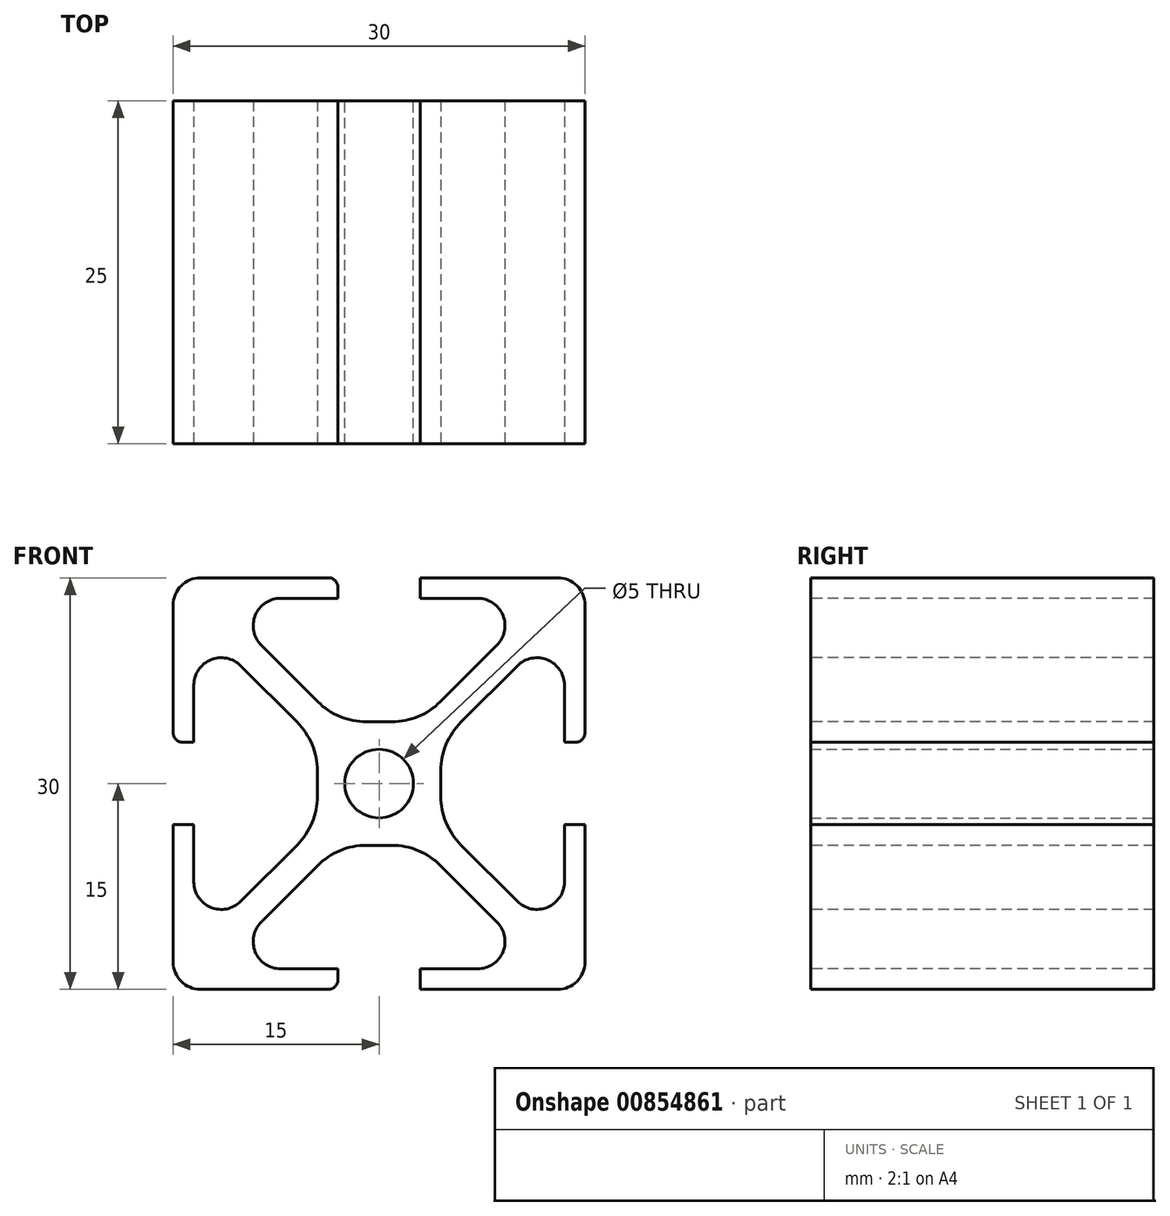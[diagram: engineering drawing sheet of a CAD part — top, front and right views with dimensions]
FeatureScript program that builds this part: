
annotation { "Feature Type Name" : "Feature", "Feature Type Description" : "" }
export const myFeature = defineFeature(function(context is Context, id is Id, definition is map)
    precondition{}
    {
        {
            var Q0;
            Q0=qCreatedBy(makeId("Front.planeOp"),FACE);
            var sketch = newSketch(context, id + "F0", { "sketchPlane" : qUnion([Q0])});
            skLineSegment(sketch, "E0.bottom", {"start": v(15, -15) * mm, "end": v(-15, -15) * mm});
            skLineSegment(sketch, "E0.top", {"start": v(15, 15) * mm, "end": v(-15, 15) * mm});
            skLineSegment(sketch, "E0.left", {"start": v(15, -15) * mm, "end": v(15, 15) * mm});
            skLineSegment(sketch, "E0.right", {"start": v(-15, -15) * mm, "end": v(-15, 15) * mm});
            skPoint(sketch, "E0.middle", {"position": v(0, 0) * mm});
            skCircle(sketch, "E1", {"center": v(0, 0) * mm, "radius": 2.5 * mm});
            skSolve(sketch);
        }
        {
            var Q0;
            Q0 = qSketchRegion(id + "F0", true);
            extrude(context, id + "F1", {"entities" : qUnion([Q0]), "endBound" : BoundingType.SYMMETRIC, "depth" : 25 * mm, "offsetDistance" : 25 * mm});
        }
        {
            var Q0;
            Q0=makeQuery(id+"F1.opExtrude","SWEPT_EDGE",EDGE,{"disambiguationData":[OSD([sQuery(id+"F0.wireOp",EDGE,"E0.top"),sQuery(id+"F0.wireOp",EDGE,"E0.left")])]});
            var Q1;
            Q1=makeQuery(id+"F1.opExtrude","SWEPT_EDGE",EDGE,{"disambiguationData":[OSD([sQuery(id+"F0.wireOp",EDGE,"E0.top"),sQuery(id+"F0.wireOp",EDGE,"E0.right")])]});
            var Q2;
            Q2=makeQuery(id+"F1.opExtrude","SWEPT_EDGE",EDGE,{"disambiguationData":[OSD([sQuery(id+"F0.wireOp",EDGE,"E0.bottom"),sQuery(id+"F0.wireOp",EDGE,"E0.right")])]});
            var Q3;
            Q3=makeQuery(id+"F1.opExtrude","SWEPT_EDGE",EDGE,{"disambiguationData":[OSD([sQuery(id+"F0.wireOp",EDGE,"E0.bottom"),sQuery(id+"F0.wireOp",EDGE,"E0.left")])]});
            fillet(context, id + "F2", {"entities" : qUnion([Q0, Q1, Q2, Q3]), "radius" : 2 * mm, "tangentPropagation" : true, "allowEdgeOverflow" : false});
        }
        {
            var Q0;
            Q0=makeQuery(id+"F1.opExtrude","CAP_FACE",FACE,{"disambiguationData":[OSD([sQuery(id+"F0.wireOp",EDGE,"E0.bottom"),sQuery(id+"F0.wireOp",EDGE,"E0.top"),sQuery(id+"F0.wireOp",EDGE,"E0.left"),sQuery(id+"F0.wireOp",EDGE,"E0.right"),sQuery(id+"F0.wireOp",EDGE,"E1")])],"isStart":false});
            var sketch = newSketch(context, id + "F3", { "sketchPlane" : qUnion([Q0])});
            skPoint(sketch, "E2.middle", {"position": v(0, 0) * mm});
            skLineSegment(sketch, "E3.left", {"start": v(4.5, 3) * mm, "end": v(4.5, -3) * mm});
            skLineSegment(sketch, "E4.bottom", {"start": v(-3, 4.5) * mm, "end": v(3, 4.5) * mm});
            skLineSegment(sketch, "E4.top", {"start": v(-3, 15) * mm, "end": v(3, 15) * mm});
            skLineSegment(sketch, "E4.left", {"start": v(-3, 4.5) * mm, "end": v(-3, 15) * mm});
            skLineSegment(sketch, "E4.right", {"start": v(3, 4.5) * mm, "end": v(3, 15) * mm});
            skLineSegment(sketch, "E5.bottom", {"start": v(4.5, 3) * mm, "end": v(15, 3) * mm});
            skLineSegment(sketch, "E5.top", {"start": v(4.5, -3) * mm, "end": v(15, -3) * mm});
            skLineSegment(sketch, "E5.right", {"start": v(15, 3) * mm, "end": v(15, -3) * mm});
            skLineSegment(sketch, "E6.bottom", {"start": v(3, -4.5) * mm, "end": v(-3, -4.5) * mm});
            skLineSegment(sketch, "E6.top", {"start": v(3, -15) * mm, "end": v(-3, -15) * mm});
            skLineSegment(sketch, "E6.left", {"start": v(3, -4.5) * mm, "end": v(3, -15) * mm});
            skLineSegment(sketch, "E6.right", {"start": v(-3, -4.5) * mm, "end": v(-3, -15) * mm});
            skLineSegment(sketch, "E7.bottom", {"start": v(-4.5, -3) * mm, "end": v(-15, -3) * mm});
            skLineSegment(sketch, "E7.top", {"start": v(-4.5, 3) * mm, "end": v(-15, 3) * mm});
            skLineSegment(sketch, "E7.left", {"start": v(-4.5, -3) * mm, "end": v(-4.5, 3) * mm});
            skLineSegment(sketch, "E7.right", {"start": v(-15, -3) * mm, "end": v(-15, 3) * mm});
            skSolve(sketch);
        }
        {
            var Q0;
            Q0 = qSketchRegion(id + "F3", true);
            extrude(context, id + "F4", {"entities" : qUnion([Q0]), "operationType" : NewBodyOperationType.REMOVE, "oppositeDirection" : true, "depth" : 25 * mm, "offsetDistance" : 25 * mm});
        }
        {
            var Q0;
            Q0 = qSketchRegion(id + "F3", true);
            extrude(context, id + "F5", {"entities" : qUnion([Q0]), "operationType" : NewBodyOperationType.REMOVE, "oppositeDirection" : true, "depth" : 25 * mm, "offsetDistance" : 25 * mm});
        }
        {
            var Q0;
            Q0=makeQuery(id+"F1.opExtrude","CAP_FACE",FACE,{"disambiguationData":[OSD([sQuery(id+"F0.wireOp",EDGE,"E0.bottom"),sQuery(id+"F0.wireOp",EDGE,"E0.top"),sQuery(id+"F0.wireOp",EDGE,"E0.left"),sQuery(id+"F0.wireOp",EDGE,"E0.right"),sQuery(id+"F0.wireOp",EDGE,"E1")])],"isStart":false});
            var sketch = newSketch(context, id + "F6", { "sketchPlane" : qUnion([Q0])});
            skPoint(sketch, "E8.middle", {"position": v(0, 0) * mm});
            skPoint(sketch, "E9.middle", {"position": v(9, 9) * mm});
            skLineSegment(sketch, "E10", {"start": v(3, 4.5) * mm, "end": v(12, 13.5) * mm});
            skLineSegment(sketch, "E11", {"start": v(4.5, 3) * mm, "end": v(13.5, 12) * mm});
            skLineSegment(sketch, "E12", {"start": v(13.5, 3) * mm, "end": v(13.5, 12) * mm});
            skLineSegment(sketch, "E13", {"start": v(3, 13.5) * mm, "end": v(12, 13.5) * mm});
            skLineSegment(sketch, "E14.MirrorCS", {"start": v(3, -13.5) * mm, "end": v(12, -13.5) * mm});
            skLineSegment(sketch, "E15.MirrorCS", {"start": v(3, -4.5) * mm, "end": v(12, -13.5) * mm});
            skLineSegment(sketch, "E16.MirrorCS", {"start": v(4.5, -3) * mm, "end": v(13.5, -12) * mm});
            skLineSegment(sketch, "E17.MirrorCS", {"start": v(13.5, -3) * mm, "end": v(13.5, -12) * mm});
            skLineSegment(sketch, "E18.MirrorCS", {"start": v(-3, 13.5) * mm, "end": v(-12, 13.5) * mm});
            skLineSegment(sketch, "E19.MirrorCS", {"start": v(-3, 4.5) * mm, "end": v(-12, 13.5) * mm});
            skLineSegment(sketch, "E20.MirrorCS", {"start": v(-4.5, 3) * mm, "end": v(-13.5, 12) * mm});
            skLineSegment(sketch, "E21.MirrorCS", {"start": v(-13.5, 3) * mm, "end": v(-13.5, 12) * mm});
            skLineSegment(sketch, "E22.MirrorCS", {"start": v(-4.5, -3) * mm, "end": v(-13.5, -12) * mm});
            skLineSegment(sketch, "E23.MirrorCS", {"start": v(-3, -4.5) * mm, "end": v(-12, -13.5) * mm});
            skLineSegment(sketch, "E24.MirrorCS", {"start": v(-3, -13.5) * mm, "end": v(-12, -13.5) * mm});
            skLineSegment(sketch, "E25.MirrorCS", {"start": v(-13.5, -3) * mm, "end": v(-13.5, -12) * mm});
            skLineSegment(sketch, "E26", {"start": v(-13.5, 3) * mm, "end": v(-4.5, 3) * mm});
            skLineSegment(sketch, "E27", {"start": v(-3, 4.5) * mm, "end": v(-3, 13.5) * mm});
            skLineSegment(sketch, "E28", {"start": v(3, 13.5) * mm, "end": v(3, 4.5) * mm});
            skLineSegment(sketch, "E29", {"start": v(4.5, 3) * mm, "end": v(13.5, 3) * mm});
            skLineSegment(sketch, "E30", {"start": v(13.5, -3) * mm, "end": v(4.5, -3) * mm});
            skLineSegment(sketch, "E31", {"start": v(3, -4.5) * mm, "end": v(3, -13.5) * mm});
            skLineSegment(sketch, "E32", {"start": v(-3, -13.5) * mm, "end": v(-3, -4.5) * mm});
            skLineSegment(sketch, "E33", {"start": v(-4.5, -3) * mm, "end": v(-13.5, -3) * mm});
            skSolve(sketch);
        }
        {
            var Q0;
            Q0 = qSketchRegion(id + "F6", true);
            extrude(context, id + "F7", {"entities" : qUnion([Q0]), "operationType" : NewBodyOperationType.REMOVE, "oppositeDirection" : true, "depth" : 25 * mm, "offsetDistance" : 25 * mm});
        }
        {
            var Q0;
            Q0=makeQuery(id+"F7.boolean.opBoolean","COPY",EDGE,{"derivedFrom":makeQuery(id+"F7.opExtrude","SWEPT_EDGE",EDGE,{"disambiguationData":[OSD([sQuery(id+"F6.wireOp",EDGE,"E23.MirrorCS"),sQuery(id+"F6.wireOp",EDGE,"E24.MirrorCS")])]})});
            var Q1;
            Q1=makeQuery(id+"F7.boolean.opBoolean","COPY",EDGE,{"derivedFrom":makeQuery(id+"F7.opExtrude","SWEPT_EDGE",EDGE,{"disambiguationData":[OSD([sQuery(id+"F6.wireOp",EDGE,"E14.MirrorCS"),sQuery(id+"F6.wireOp",EDGE,"E15.MirrorCS")])]})});
            var Q2;
            Q2=makeQuery(id+"F7.boolean.opBoolean","COPY",EDGE,{"derivedFrom":makeQuery(id+"F7.opExtrude","SWEPT_EDGE",EDGE,{"disambiguationData":[OSD([sQuery(id+"F6.wireOp",EDGE,"E16.MirrorCS"),sQuery(id+"F6.wireOp",EDGE,"E17.MirrorCS")])]})});
            var Q3;
            Q3=makeQuery(id+"F7.boolean.opBoolean","COPY",EDGE,{"derivedFrom":makeQuery(id+"F7.opExtrude","SWEPT_EDGE",EDGE,{"disambiguationData":[OSD([sQuery(id+"F6.wireOp",EDGE,"E22.MirrorCS"),sQuery(id+"F6.wireOp",EDGE,"E25.MirrorCS")])]})});
            var Q4;
            Q4=makeQuery(id+"F7.boolean.opBoolean","COPY",EDGE,{"derivedFrom":makeQuery(id+"F7.opExtrude","SWEPT_EDGE",EDGE,{"disambiguationData":[OSD([sQuery(id+"F6.wireOp",EDGE,"E11"),sQuery(id+"F6.wireOp",EDGE,"E12")])]})});
            var Q5;
            Q5=makeQuery(id+"F7.boolean.opBoolean","COPY",EDGE,{"derivedFrom":makeQuery(id+"F7.opExtrude","SWEPT_EDGE",EDGE,{"disambiguationData":[OSD([sQuery(id+"F6.wireOp",EDGE,"E10"),sQuery(id+"F6.wireOp",EDGE,"E13")])]})});
            var Q6;
            Q6=makeQuery(id+"F7.boolean.opBoolean","COPY",EDGE,{"derivedFrom":makeQuery(id+"F7.opExtrude","SWEPT_EDGE",EDGE,{"disambiguationData":[OSD([sQuery(id+"F6.wireOp",EDGE,"E20.MirrorCS"),sQuery(id+"F6.wireOp",EDGE,"E21.MirrorCS")])]})});
            var Q7;
            Q7=makeQuery(id+"F7.boolean.opBoolean","COPY",EDGE,{"derivedFrom":makeQuery(id+"F7.opExtrude","SWEPT_EDGE",EDGE,{"disambiguationData":[OSD([sQuery(id+"F6.wireOp",EDGE,"E18.MirrorCS"),sQuery(id+"F6.wireOp",EDGE,"E19.MirrorCS")])]})});
            fillet(context, id + "F8", {"entities" : qUnion([Q0, Q1, Q2, Q3, Q4, Q5, Q6, Q7]), "radius" : 2 * mm, "tangentPropagation" : true, "allowEdgeOverflow" : false});
        }
        {
            var Q0;
            Q0=makeQuery(id+"F7.boolean.opBoolean","COPY",EDGE,{"derivedFrom":makeQuery(id+"F7.opExtrude","SWEPT_EDGE",EDGE,{"disambiguationData":[OSD([sQuery(id+"F3.wireOp",EDGE,"E5.bottom"),sQuery(id+"F6.wireOp",EDGE,"E12"),sQuery(id+"F6.wireOp",EDGE,"E29")])]})});
            var Q1;
            Q1=makeQuery(id+"F4.boolean.opBoolean","COPY",EDGE,{"derivedFrom":makeQuery(id+"F4.opExtrude","SWEPT_EDGE",EDGE,{"disambiguationData":[OSD([sQuery(id+"F0.wireOp",EDGE,"E0.left"),sQuery(id+"F3.wireOp",EDGE,"E5.bottom"),sQuery(id+"F3.wireOp",EDGE,"E5.right")])]})});
            var Q2;
            Q2=makeQuery(id+"F4.boolean.opBoolean","COPY",EDGE,{"derivedFrom":makeQuery(id+"F4.opExtrude","SWEPT_EDGE",EDGE,{"disambiguationData":[OSD([sQuery(id+"F0.wireOp",EDGE,"E0.left"),sQuery(id+"F3.wireOp",EDGE,"E5.top"),sQuery(id+"F3.wireOp",EDGE,"E5.right")])]})});
            var Q3;
            Q3=makeQuery(id+"F7.boolean.opBoolean","COPY",EDGE,{"derivedFrom":makeQuery(id+"F7.opExtrude","SWEPT_EDGE",EDGE,{"disambiguationData":[OSD([sQuery(id+"F3.wireOp",EDGE,"E5.top"),sQuery(id+"F6.wireOp",EDGE,"E17.MirrorCS"),sQuery(id+"F6.wireOp",EDGE,"E30")])]})});
            var Q4;
            Q4=makeQuery(id+"F4.boolean.opBoolean","COPY",EDGE,{"derivedFrom":makeQuery(id+"F4.opExtrude","SWEPT_EDGE",EDGE,{"disambiguationData":[OSD([sQuery(id+"F0.wireOp",EDGE,"E0.bottom"),sQuery(id+"F3.wireOp",EDGE,"E6.top"),sQuery(id+"F3.wireOp",EDGE,"E6.left")])]})});
            var Q5;
            Q5=makeQuery(id+"F4.boolean.opBoolean","COPY",EDGE,{"derivedFrom":makeQuery(id+"F4.opExtrude","SWEPT_EDGE",EDGE,{"disambiguationData":[OSD([sQuery(id+"F0.wireOp",EDGE,"E0.bottom"),sQuery(id+"F3.wireOp",EDGE,"E6.top"),sQuery(id+"F3.wireOp",EDGE,"E6.right")])]})});
            var Q6;
            Q6=makeQuery(id+"F7.boolean.opBoolean","COPY",EDGE,{"derivedFrom":makeQuery(id+"F7.opExtrude","SWEPT_EDGE",EDGE,{"disambiguationData":[OSD([sQuery(id+"F3.wireOp",EDGE,"E6.left"),sQuery(id+"F6.wireOp",EDGE,"E14.MirrorCS"),sQuery(id+"F6.wireOp",EDGE,"E31")])]})});
            var Q7;
            Q7=makeQuery(id+"F7.boolean.opBoolean","COPY",EDGE,{"derivedFrom":makeQuery(id+"F7.opExtrude","SWEPT_EDGE",EDGE,{"disambiguationData":[OSD([sQuery(id+"F3.wireOp",EDGE,"E6.right"),sQuery(id+"F6.wireOp",EDGE,"E24.MirrorCS"),sQuery(id+"F6.wireOp",EDGE,"E32")])]})});
            var Q8;
            Q8=makeQuery(id+"F4.boolean.opBoolean","COPY",EDGE,{"derivedFrom":makeQuery(id+"F4.opExtrude","SWEPT_EDGE",EDGE,{"disambiguationData":[OSD([sQuery(id+"F0.wireOp",EDGE,"E0.right"),sQuery(id+"F3.wireOp",EDGE,"E7.bottom"),sQuery(id+"F3.wireOp",EDGE,"E7.right")])]})});
            var Q9;
            Q9=makeQuery(id+"F7.boolean.opBoolean","COPY",EDGE,{"derivedFrom":makeQuery(id+"F7.opExtrude","SWEPT_EDGE",EDGE,{"disambiguationData":[OSD([sQuery(id+"F3.wireOp",EDGE,"E7.bottom"),sQuery(id+"F6.wireOp",EDGE,"E25.MirrorCS"),sQuery(id+"F6.wireOp",EDGE,"E33")])]})});
            var Q10;
            Q10=makeQuery(id+"F4.boolean.opBoolean","COPY",EDGE,{"derivedFrom":makeQuery(id+"F4.opExtrude","SWEPT_EDGE",EDGE,{"disambiguationData":[OSD([sQuery(id+"F0.wireOp",EDGE,"E0.right"),sQuery(id+"F3.wireOp",EDGE,"E7.top"),sQuery(id+"F3.wireOp",EDGE,"E7.right")])]})});
            var Q11;
            Q11=makeQuery(id+"F7.boolean.opBoolean","COPY",EDGE,{"derivedFrom":makeQuery(id+"F7.opExtrude","SWEPT_EDGE",EDGE,{"disambiguationData":[OSD([sQuery(id+"F3.wireOp",EDGE,"E7.top"),sQuery(id+"F6.wireOp",EDGE,"E21.MirrorCS"),sQuery(id+"F6.wireOp",EDGE,"E26")])]})});
            var Q12;
            Q12=makeQuery(id+"F7.boolean.opBoolean","COPY",EDGE,{"derivedFrom":makeQuery(id+"F7.opExtrude","SWEPT_EDGE",EDGE,{"disambiguationData":[OSD([sQuery(id+"F3.wireOp",EDGE,"E4.right"),sQuery(id+"F6.wireOp",EDGE,"E13"),sQuery(id+"F6.wireOp",EDGE,"E28")])]})});
            var Q13;
            Q13=makeQuery(id+"F4.boolean.opBoolean","COPY",EDGE,{"derivedFrom":makeQuery(id+"F4.opExtrude","SWEPT_EDGE",EDGE,{"disambiguationData":[OSD([sQuery(id+"F0.wireOp",EDGE,"E0.top"),sQuery(id+"F3.wireOp",EDGE,"E4.top"),sQuery(id+"F3.wireOp",EDGE,"E4.right")])]})});
            var Q14;
            Q14=makeQuery(id+"F4.boolean.opBoolean","COPY",EDGE,{"derivedFrom":makeQuery(id+"F4.opExtrude","SWEPT_EDGE",EDGE,{"disambiguationData":[OSD([sQuery(id+"F0.wireOp",EDGE,"E0.top"),sQuery(id+"F3.wireOp",EDGE,"E4.top"),sQuery(id+"F3.wireOp",EDGE,"E4.left")])]})});
            var Q15;
            Q15=makeQuery(id+"F7.boolean.opBoolean","COPY",EDGE,{"derivedFrom":makeQuery(id+"F7.opExtrude","SWEPT_EDGE",EDGE,{"disambiguationData":[OSD([sQuery(id+"F3.wireOp",EDGE,"E4.left"),sQuery(id+"F6.wireOp",EDGE,"E18.MirrorCS"),sQuery(id+"F6.wireOp",EDGE,"E27")])]})});
            fillet(context, id + "F9", {"entities" : qUnion([Q0, Q1, Q2, Q3, Q4, Q5, Q6, Q7, Q8, Q9, Q10, Q11, Q12, Q13, Q14, Q15]), "radius" : 0.7 * mm, "tangentPropagation" : true, "allowEdgeOverflow" : false});
        }
        {
            var Q0;
            {var subQ0=sQuery(id+"F3.wireOp",EDGE,"E3.left");Q0=makeQuery(id+"F7.boolean.opBoolean","MERGE",EDGE,{"derivedFrom":[makeQuery(id+"F4.boolean.opBoolean","COPY",EDGE,{"derivedFrom":makeQuery(id+"F4.opExtrude","SWEPT_EDGE",EDGE,{"disambiguationData":[OSD([sQuery(id+"F3.wireOp",EDGE,"E5.top"),subQ0])]})}),makeQuery(id+"F7.opExtrude","SWEPT_EDGE",EDGE,{"disambiguationData":[OSD([subQ0,sQuery(id+"F6.wireOp",EDGE,"E16.MirrorCS"),sQuery(id+"F6.wireOp",EDGE,"E30")])]})]});}
            var Q1;
            {var subQ0=sQuery(id+"F3.wireOp",EDGE,"E3.left");Q1=makeQuery(id+"F7.boolean.opBoolean","MERGE",EDGE,{"derivedFrom":[makeQuery(id+"F4.boolean.opBoolean","COPY",EDGE,{"derivedFrom":makeQuery(id+"F4.opExtrude","SWEPT_EDGE",EDGE,{"disambiguationData":[OSD([sQuery(id+"F3.wireOp",EDGE,"E5.bottom"),subQ0])]})}),makeQuery(id+"F7.opExtrude","SWEPT_EDGE",EDGE,{"disambiguationData":[OSD([subQ0,sQuery(id+"F6.wireOp",EDGE,"E11"),sQuery(id+"F6.wireOp",EDGE,"E29")])]})]});}
            var Q2;
            {var subQ0=sQuery(id+"F3.wireOp",EDGE,"E6.bottom");Q2=makeQuery(id+"F7.boolean.opBoolean","MERGE",EDGE,{"derivedFrom":[makeQuery(id+"F4.boolean.opBoolean","COPY",EDGE,{"derivedFrom":makeQuery(id+"F4.opExtrude","SWEPT_EDGE",EDGE,{"disambiguationData":[OSD([subQ0,sQuery(id+"F3.wireOp",EDGE,"E6.right")])]})}),makeQuery(id+"F7.opExtrude","SWEPT_EDGE",EDGE,{"disambiguationData":[OSD([subQ0,sQuery(id+"F6.wireOp",EDGE,"E23.MirrorCS"),sQuery(id+"F6.wireOp",EDGE,"E32")])]})]});}
            var Q3;
            {var subQ0=sQuery(id+"F3.wireOp",EDGE,"E6.bottom");Q3=makeQuery(id+"F7.boolean.opBoolean","MERGE",EDGE,{"derivedFrom":[makeQuery(id+"F4.boolean.opBoolean","COPY",EDGE,{"derivedFrom":makeQuery(id+"F4.opExtrude","SWEPT_EDGE",EDGE,{"disambiguationData":[OSD([subQ0,sQuery(id+"F3.wireOp",EDGE,"E6.left")])]})}),makeQuery(id+"F7.opExtrude","SWEPT_EDGE",EDGE,{"disambiguationData":[OSD([subQ0,sQuery(id+"F6.wireOp",EDGE,"E15.MirrorCS"),sQuery(id+"F6.wireOp",EDGE,"E31")])]})]});}
            var Q4;
            {var subQ0=sQuery(id+"F3.wireOp",EDGE,"E7.left");Q4=makeQuery(id+"F7.boolean.opBoolean","MERGE",EDGE,{"derivedFrom":[makeQuery(id+"F4.boolean.opBoolean","COPY",EDGE,{"derivedFrom":makeQuery(id+"F4.opExtrude","SWEPT_EDGE",EDGE,{"disambiguationData":[OSD([sQuery(id+"F3.wireOp",EDGE,"E7.bottom"),subQ0])]})}),makeQuery(id+"F7.opExtrude","SWEPT_EDGE",EDGE,{"disambiguationData":[OSD([subQ0,sQuery(id+"F6.wireOp",EDGE,"E22.MirrorCS"),sQuery(id+"F6.wireOp",EDGE,"E33")])]})]});}
            var Q5;
            {var subQ0=sQuery(id+"F3.wireOp",EDGE,"E7.left");Q5=makeQuery(id+"F7.boolean.opBoolean","MERGE",EDGE,{"derivedFrom":[makeQuery(id+"F4.boolean.opBoolean","COPY",EDGE,{"derivedFrom":makeQuery(id+"F4.opExtrude","SWEPT_EDGE",EDGE,{"disambiguationData":[OSD([sQuery(id+"F3.wireOp",EDGE,"E7.top"),subQ0])]})}),makeQuery(id+"F7.opExtrude","SWEPT_EDGE",EDGE,{"disambiguationData":[OSD([subQ0,sQuery(id+"F6.wireOp",EDGE,"E20.MirrorCS"),sQuery(id+"F6.wireOp",EDGE,"E26")])]})]});}
            var Q6;
            {var subQ0=sQuery(id+"F3.wireOp",EDGE,"E4.bottom");Q6=makeQuery(id+"F7.boolean.opBoolean","MERGE",EDGE,{"derivedFrom":[makeQuery(id+"F4.boolean.opBoolean","COPY",EDGE,{"derivedFrom":makeQuery(id+"F4.opExtrude","SWEPT_EDGE",EDGE,{"disambiguationData":[OSD([subQ0,sQuery(id+"F3.wireOp",EDGE,"E4.right")])]})}),makeQuery(id+"F7.opExtrude","SWEPT_EDGE",EDGE,{"disambiguationData":[OSD([subQ0,sQuery(id+"F6.wireOp",EDGE,"E10"),sQuery(id+"F6.wireOp",EDGE,"E28")])]})]});}
            var Q7;
            {var subQ0=sQuery(id+"F3.wireOp",EDGE,"E4.bottom");Q7=makeQuery(id+"F7.boolean.opBoolean","MERGE",EDGE,{"derivedFrom":[makeQuery(id+"F4.boolean.opBoolean","COPY",EDGE,{"derivedFrom":makeQuery(id+"F4.opExtrude","SWEPT_EDGE",EDGE,{"disambiguationData":[OSD([subQ0,sQuery(id+"F3.wireOp",EDGE,"E4.left")])]})}),makeQuery(id+"F7.opExtrude","SWEPT_EDGE",EDGE,{"disambiguationData":[OSD([subQ0,sQuery(id+"F6.wireOp",EDGE,"E19.MirrorCS"),sQuery(id+"F6.wireOp",EDGE,"E27")])]})]});}
            fillet(context, id + "F10", {"entities" : qUnion([Q0, Q1, Q2, Q3, Q4, Q5, Q6, Q7]), "radius" : 5 * mm, "tangentPropagation" : true, "allowEdgeOverflow" : false});
        }
    });
